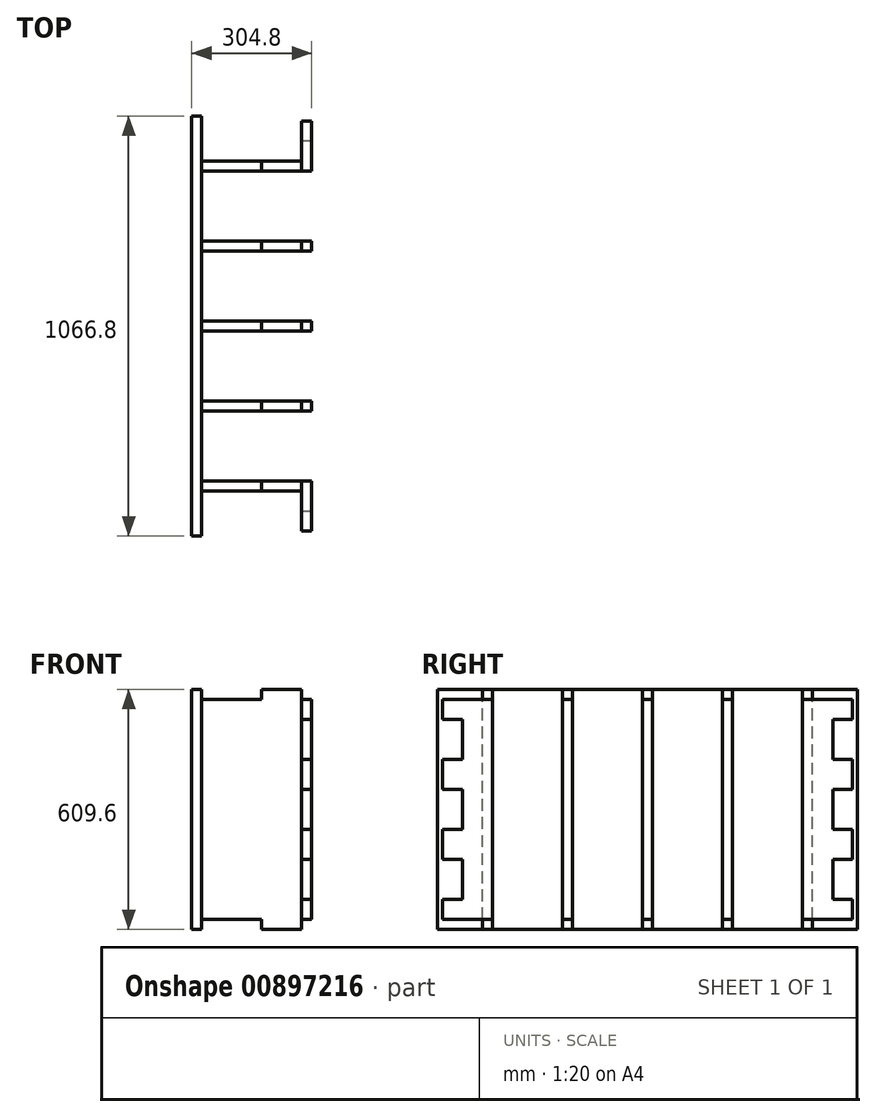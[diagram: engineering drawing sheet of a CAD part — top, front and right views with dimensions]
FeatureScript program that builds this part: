
annotation { "Feature Type Name" : "Feature", "Feature Type Description" : "" }
export const myFeature = defineFeature(function(context is Context, id is Id, definition is map)
    precondition{}
    {
        {
            var Q0;
            Q0=qCreatedBy(makeId("Top.planeOp"),FACE);
            var sketch = newSketch(context, id + "F0", { "sketchPlane" : qUnion([Q0])});
            skLineSegment(sketch, "E0.top", {"start": v(0, 838.2) * mm, "end": v(304.8, 838.2) * mm});
            skLineSegment(sketch, "E0.left", {"start": v(0, 419.1) * mm, "end": v(0, 838.2) * mm});
            skLineSegment(sketch, "E0.right", {"start": v(304.8, 419.1) * mm, "end": v(304.8, 431.8) * mm});
            skLineSegment(sketch, "E1", {"start": v(25.4, 812.8) * mm, "end": v(304.8, 812.8) * mm});
            skLineSegment(sketch, "E2", {"start": v(0, 419.1) * mm, "end": v(416.46, 419.1) * mm, "construction": true});
            skLineSegment(sketch, "E3", {"start": v(25.4, 812.8) * mm, "end": v(25.4, 635) * mm});
            skLineSegment(sketch, "E4", {"start": v(25.4, 431.8) * mm, "end": v(304.8, 431.8) * mm});
            skPoint(sketch, "E0.bottom.start.orphan", {"position": v(0, 0) * mm});
            skLineSegment(sketch, "E5.trimOffspring", {"start": v(304.8, 812.8) * mm, "end": v(304.8, 838.2) * mm});
            skLineSegment(sketch, "E6.MirrorCS", {"start": v(304.8, 25.4) * mm, "end": v(304.8, 0) * mm});
            skLineSegment(sketch, "E7.MirrorCS", {"start": v(304.8, 419.1) * mm, "end": v(304.8, 406.4) * mm});
            skLineSegment(sketch, "E8.MirrorCS", {"start": v(25.4, 25.4) * mm, "end": v(304.8, 25.4) * mm});
            skLineSegment(sketch, "E9.MirrorCS", {"start": v(0, 0) * mm, "end": v(304.8, 0) * mm});
            skLineSegment(sketch, "E10.MirrorCS", {"start": v(25.4, 406.4) * mm, "end": v(304.8, 406.4) * mm});
            skLineSegment(sketch, "E11.MirrorCS", {"start": v(25.4, 25.4) * mm, "end": v(25.4, 203.2) * mm});
            skLineSegment(sketch, "E12.MirrorCS", {"start": v(0, 419.1) * mm, "end": v(0, 0) * mm});
            skPoint(sketch, "E13.orphan", {"position": v(25.4, 419.1) * mm});
            skLineSegment(sketch, "E14.0.1.0", {"start": v(25.4, 635) * mm, "end": v(304.8, 635) * mm});
            skLineSegment(sketch, "E14.0.1.1", {"start": v(304.8, 622.3) * mm, "end": v(304.8, 635) * mm});
            skLineSegment(sketch, "E14.0.1.2", {"start": v(304.8, 622.3) * mm, "end": v(304.8, 609.6) * mm});
            skLineSegment(sketch, "E14.0.1.3", {"start": v(25.4, 609.6) * mm, "end": v(304.8, 609.6) * mm});
            skLineSegment(sketch, "E14.direction1", {"start": v(25.4, 431.8) * mm, "end": v(50.8, 431.8) * mm, "construction": true});
            skLineSegment(sketch, "E14.direction2", {"start": v(25.4, 431.8) * mm, "end": v(25.4, 609.6) * mm, "construction": true});
            skLineSegment(sketch, "E15.trimOffspring", {"start": v(25.4, 609.6) * mm, "end": v(25.4, 431.8) * mm});
            skLineSegment(sketch, "E16.MirrorCS", {"start": v(25.4, 203.2) * mm, "end": v(304.8, 203.2) * mm});
            skLineSegment(sketch, "E17.MirrorCS", {"start": v(25.4, 228.6) * mm, "end": v(304.8, 228.6) * mm});
            skLineSegment(sketch, "E18.MirrorCS", {"start": v(304.8, 215.9) * mm, "end": v(304.8, 203.2) * mm});
            skLineSegment(sketch, "E19.MirrorCS", {"start": v(304.8, 215.9) * mm, "end": v(304.8, 228.6) * mm});
            skLineSegment(sketch, "E20.trimOffspring", {"start": v(25.4, 228.6) * mm, "end": v(25.4, 406.4) * mm});
            skSolve(sketch);
        }
        {
            var Q0;
            Q0=qSketchRegion(id+"F0",true);
            extrude(context, id + "F1", {"entities" : qUnion([Q0]), "oppositeDirection" : true, "depth" : 609.6 * mm, "offsetDistance" : 25.4 * mm});
        }
        {
            var Q0;
            Q0=makeQuery(id+"F0.imprint","IMPRINT",FACE,{"disambiguationData":[TD([[makeQuery(id+"F0.imprint","IMPRINT",EDGE,{"derivedFrom":sQuery(id+"F0.wireOp",EDGE,"E0.top")}),-1.0]])]});
            var sketch = newSketch(context, id + "F2", { "sketchPlane" : qUnion([Q0])});
            skLineSegment(sketch, "E21.bottom", {"start": v(304.8, 838.2) * mm, "end": v(279.4, 838.2) * mm});
            skLineSegment(sketch, "E21.top", {"start": v(304.8, 939.8) * mm, "end": v(279.4, 939.8) * mm});
            skLineSegment(sketch, "E21.left", {"start": v(304.8, 838.2) * mm, "end": v(304.8, 939.8) * mm});
            skLineSegment(sketch, "E21.right", {"start": v(279.4, 838.2) * mm, "end": v(279.4, 939.8) * mm});
            skLineSegment(sketch, "E22.bottom", {"start": v(0, 838.2) * mm, "end": v(25.4, 838.2) * mm});
            skLineSegment(sketch, "E22.top", {"start": v(0, 952.5) * mm, "end": v(25.4, 952.5) * mm});
            skLineSegment(sketch, "E22.left", {"start": v(0, 838.2) * mm, "end": v(0, 952.5) * mm});
            skLineSegment(sketch, "E22.right", {"start": v(25.4, 838.2) * mm, "end": v(25.4, 952.5) * mm});
            skLineSegment(sketch, "E23.MirrorCS", {"start": v(0, -114.3) * mm, "end": v(25.4, -114.3) * mm});
            skLineSegment(sketch, "E24.MirrorCS", {"start": v(304.8, -101.6) * mm, "end": v(279.4, -101.6) * mm});
            skLineSegment(sketch, "E25.MirrorCS", {"start": v(0, 0) * mm, "end": v(0, -114.3) * mm});
            skLineSegment(sketch, "E26.MirrorCS", {"start": v(304.8, 0) * mm, "end": v(279.4, 0) * mm});
            skLineSegment(sketch, "E27.MirrorCS", {"start": v(0, 0) * mm, "end": v(25.4, 0) * mm});
            skLineSegment(sketch, "E28.MirrorCS", {"start": v(304.8, 0) * mm, "end": v(304.8, -101.6) * mm});
            skLineSegment(sketch, "E29.MirrorCS", {"start": v(279.4, 0) * mm, "end": v(279.4, -101.6) * mm});
            skLineSegment(sketch, "E30.MirrorCS", {"start": v(25.4, 0) * mm, "end": v(25.4, -114.3) * mm});
            skSolve(sketch);
        }
        {
            var Q0;
            Q0=qSketchRegion(id+"F2",true);
            extrude(context, id + "F3", {"entities" : qUnion([Q0]), "operationType" : NewBodyOperationType.ADD, "oppositeDirection" : true, "depth" : 609.6 * mm, "offsetDistance" : 25.4 * mm});
        }
        {
            var Q0;
            Q0=qCreatedBy(makeId("Front.planeOp"),FACE);
            var sketch = newSketch(context, id + "F4", { "sketchPlane" : qUnion([Q0])});
            skLineSegment(sketch, "E31.bottom", {"start": v(25.4, 0) * mm, "end": v(177.8, 0) * mm});
            skLineSegment(sketch, "E31.top", {"start": v(25.4, -25.4) * mm, "end": v(177.8, -25.4) * mm});
            skLineSegment(sketch, "E31.left", {"start": v(25.4, 0) * mm, "end": v(25.4, -25.4) * mm});
            skLineSegment(sketch, "E31.right", {"start": v(177.8, 0) * mm, "end": v(177.8, -25.4) * mm});
            skLineSegment(sketch, "E32.direction1", {"start": v(25.4, -25.4) * mm, "end": v(50.8, -25.4) * mm, "construction": true});
            skLineSegment(sketch, "E33.bottom", {"start": v(304.8, 0) * mm, "end": v(279.4, 0) * mm});
            skLineSegment(sketch, "E33.top", {"start": v(304.8, -25.4) * mm, "end": v(279.4, -25.4) * mm});
            skLineSegment(sketch, "E33.left", {"start": v(304.8, 0) * mm, "end": v(304.8, -25.4) * mm});
            skLineSegment(sketch, "E33.right", {"start": v(279.4, 0) * mm, "end": v(279.4, -25.4) * mm});
            skLineSegment(sketch, "E34.bottom", {"start": v(25.4, -609.6) * mm, "end": v(177.8, -609.6) * mm});
            skLineSegment(sketch, "E34.top", {"start": v(25.4, -584.2) * mm, "end": v(177.8, -584.2) * mm});
            skLineSegment(sketch, "E34.left", {"start": v(25.4, -609.6) * mm, "end": v(25.4, -584.2) * mm});
            skLineSegment(sketch, "E34.right", {"start": v(177.8, -609.6) * mm, "end": v(177.8, -584.2) * mm});
            skLineSegment(sketch, "E35.bottom", {"start": v(304.8, -609.6) * mm, "end": v(279.4, -609.6) * mm});
            skLineSegment(sketch, "E35.top", {"start": v(304.8, -584.2) * mm, "end": v(279.4, -584.2) * mm});
            skLineSegment(sketch, "E35.left", {"start": v(304.8, -609.6) * mm, "end": v(304.8, -584.2) * mm});
            skLineSegment(sketch, "E35.right", {"start": v(279.4, -609.6) * mm, "end": v(279.4, -584.2) * mm});
            skSolve(sketch);
        }
        {
            var Q0;
            Q0 = qSketchRegion(id + "F4", true);
            extrude(context, id + "F5", {"entities" : qUnion([Q0]), "operationType" : NewBodyOperationType.REMOVE, "oppositeDirection" : true, "depth" : 2032 * mm, "offsetDistance" : 25.4 * mm, "symmetric" : true});
        }
        {
            var Q0;
            Q0=makeQuery(id+"F3.boolean.opBoolean","MERGE",FACE,{"derivedFrom":[makeQuery(id+"F1.opExtrude","SWEPT_FACE",FACE,{"disambiguationData":[OSD([sQuery(id+"F0.wireOp",EDGE,"E6.MirrorCS")])]}),makeQuery(id+"F3.opExtrude","SWEPT_FACE",FACE,{"disambiguationData":[OSD([sQuery(id+"F2.wireOp",EDGE,"E28.MirrorCS")])]})]});
            var sketch = newSketch(context, id + "F6", { "sketchPlane" : qUnion([Q0])});
            skPoint(sketch, "E36.startSnap0", {"position": v(-101.6, -304.8) * mm});
            skLineSegment(sketch, "E37", {"start": v(-101.6, -304.8) * mm, "end": v(-101.6, -254) * mm});
            skLineSegment(sketch, "E38", {"start": v(-101.6, -254) * mm, "end": v(-50.8, -254) * mm});
            skLineSegment(sketch, "E39", {"start": v(-50.8, -254) * mm, "end": v(-50.8, -304.8) * mm});
            skLineSegment(sketch, "E40", {"start": v(419.53, 0) * mm, "end": v(419.53, -619.5) * mm, "construction": true});
            skLineSegment(sketch, "E41", {"start": v(-101.6, -304.8) * mm, "end": v(1120.21, -304.8) * mm, "construction": true});
            skLineSegment(sketch, "E42.MirrorCS", {"start": v(-101.6, -304.8) * mm, "end": v(-101.6, -355.6) * mm});
            skLineSegment(sketch, "E43.MirrorCS", {"start": v(-101.6, -355.6) * mm, "end": v(-50.8, -355.6) * mm});
            skLineSegment(sketch, "E44.MirrorCS", {"start": v(-50.8, -355.6) * mm, "end": v(-50.8, -304.8) * mm});
            skPoint(sketch, "E45.0.1.0", {"position": v(-101.6, -127) * mm});
            skLineSegment(sketch, "E45.0.1.1", {"start": v(-50.8, -76.2) * mm, "end": v(-50.8, -127) * mm});
            skLineSegment(sketch, "E45.0.1.2", {"start": v(-101.6, -127) * mm, "end": v(-101.6, -76.2) * mm});
            skLineSegment(sketch, "E45.0.1.3", {"start": v(-101.6, -127) * mm, "end": v(-101.6, -177.8) * mm});
            skLineSegment(sketch, "E45.0.1.4", {"start": v(-50.8, -177.8) * mm, "end": v(-50.8, -127) * mm});
            skLineSegment(sketch, "E45.0.1.5", {"start": v(-101.6, -177.8) * mm, "end": v(-50.8, -177.8) * mm});
            skLineSegment(sketch, "E45.0.1.6", {"start": v(-101.6, -76.2) * mm, "end": v(-50.8, -76.2) * mm});
            skLineSegment(sketch, "E45.direction1", {"start": v(-101.6, -355.6) * mm, "end": v(-76.2, -355.6) * mm, "construction": true});
            skLineSegment(sketch, "E45.direction2", {"start": v(-101.6, -355.6) * mm, "end": v(-101.6, -177.8) * mm, "construction": true});
            skLineSegment(sketch, "E46.0.1.0", {"start": v(-50.8, -533.4) * mm, "end": v(-50.8, -482.6) * mm});
            skLineSegment(sketch, "E46.0.1.1", {"start": v(-101.6, -533.4) * mm, "end": v(-50.8, -533.4) * mm});
            skPoint(sketch, "E46.0.1.2", {"position": v(-101.6, -482.6) * mm});
            skLineSegment(sketch, "E46.0.1.3", {"start": v(-101.6, -482.6) * mm, "end": v(-101.6, -533.4) * mm});
            skLineSegment(sketch, "E46.0.1.4", {"start": v(-101.6, -431.8) * mm, "end": v(-50.8, -431.8) * mm});
            skLineSegment(sketch, "E46.0.1.5", {"start": v(-50.8, -431.8) * mm, "end": v(-50.8, -482.6) * mm});
            skLineSegment(sketch, "E46.0.1.6", {"start": v(-101.6, -533.4) * mm, "end": v(-76.2, -533.4) * mm, "construction": true});
            skLineSegment(sketch, "E46.0.1.7", {"start": v(-101.6, -482.6) * mm, "end": v(-101.6, -431.8) * mm});
            skLineSegment(sketch, "E46.direction2", {"start": v(-101.6, -355.6) * mm, "end": v(-101.6, -533.4) * mm, "construction": true});
            skLineSegment(sketch, "E47.MirrorCS", {"start": v(940.66, -355.6) * mm, "end": v(915.26, -355.6) * mm, "construction": true});
            skLineSegment(sketch, "E48.MirrorCS", {"start": v(940.66, -355.6) * mm, "end": v(889.86, -355.6) * mm});
            skLineSegment(sketch, "E49.MirrorCS", {"start": v(940.66, -482.6) * mm, "end": v(940.66, -533.4) * mm});
            skLineSegment(sketch, "E50.MirrorCS", {"start": v(940.66, -482.6) * mm, "end": v(940.66, -431.8) * mm});
            skLineSegment(sketch, "E51.MirrorCS", {"start": v(940.66, -304.8) * mm, "end": v(940.66, -355.6) * mm});
            skLineSegment(sketch, "E52.MirrorCS", {"start": v(940.66, -533.4) * mm, "end": v(915.26, -533.4) * mm, "construction": true});
            skLineSegment(sketch, "E53.MirrorCS", {"start": v(940.66, -254) * mm, "end": v(889.86, -254) * mm});
            skLineSegment(sketch, "E54.MirrorCS", {"start": v(940.66, -533.4) * mm, "end": v(889.86, -533.4) * mm});
            skLineSegment(sketch, "E55.MirrorCS", {"start": v(940.66, -304.8) * mm, "end": v(940.66, -254) * mm});
            skLineSegment(sketch, "E56.MirrorCS", {"start": v(940.66, -177.8) * mm, "end": v(889.86, -177.8) * mm});
            skLineSegment(sketch, "E57.MirrorCS", {"start": v(889.86, -355.6) * mm, "end": v(889.86, -304.8) * mm});
            skLineSegment(sketch, "E58.MirrorCS", {"start": v(940.66, -76.2) * mm, "end": v(889.86, -76.2) * mm});
            skPoint(sketch, "E59.MirrorP", {"position": v(940.66, -127) * mm});
            skPoint(sketch, "E60.MirrorP", {"position": v(940.66, -304.8) * mm});
            skLineSegment(sketch, "E61.MirrorCS", {"start": v(889.86, -431.8) * mm, "end": v(889.86, -482.6) * mm});
            skLineSegment(sketch, "E62.MirrorCS", {"start": v(940.66, -431.8) * mm, "end": v(889.86, -431.8) * mm});
            skLineSegment(sketch, "E63.MirrorCS", {"start": v(940.66, -127) * mm, "end": v(940.66, -177.8) * mm});
            skLineSegment(sketch, "E64.MirrorCS", {"start": v(889.86, -76.2) * mm, "end": v(889.86, -127) * mm});
            skPoint(sketch, "E65.MirrorP", {"position": v(940.66, -482.6) * mm});
            skLineSegment(sketch, "E66.MirrorCS", {"start": v(940.66, -355.6) * mm, "end": v(940.66, -177.8) * mm, "construction": true});
            skLineSegment(sketch, "E67.MirrorCS", {"start": v(889.86, -177.8) * mm, "end": v(889.86, -127) * mm});
            skLineSegment(sketch, "E68.MirrorCS", {"start": v(889.86, -533.4) * mm, "end": v(889.86, -482.6) * mm});
            skLineSegment(sketch, "E69.MirrorCS", {"start": v(889.86, -254) * mm, "end": v(889.86, -304.8) * mm});
            skLineSegment(sketch, "E70.MirrorCS", {"start": v(940.66, -355.6) * mm, "end": v(940.66, -533.4) * mm, "construction": true});
            skLineSegment(sketch, "E71.MirrorCS", {"start": v(940.66, -127) * mm, "end": v(940.66, -76.2) * mm});
            skSolve(sketch);
        }
        {
            var Q0;
            Q0 = qSketchRegion(id + "F6", true);
            extrude(context, id + "F7", {"entities" : qUnion([Q0]), "operationType" : NewBodyOperationType.REMOVE, "endBound" : BoundingType.UP_TO_NEXT, "oppositeDirection" : true, "depth" : 25.4 * mm, "offsetDistance" : 25.4 * mm});
        }
        {
            var Q0;
            Q0 = qSketchRegion(id + "F6", true);
            extrude(context, id + "F8", {"entities" : qUnion([Q0]), "operationType" : NewBodyOperationType.REMOVE, "oppositeDirection" : true, "depth" : 25.4 * mm, "offsetDistance" : 25.4 * mm});
        }
    });
